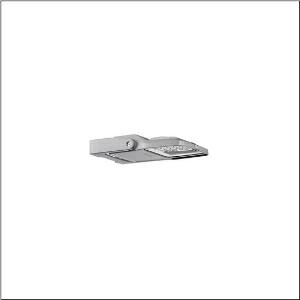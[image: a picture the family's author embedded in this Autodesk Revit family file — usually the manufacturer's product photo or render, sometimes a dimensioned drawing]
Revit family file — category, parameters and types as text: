
# Revit family: floodlight_fl_21_iq_micro___pl61_5xa7761a2c2a_8a4e
name_source: partatom
category: Lighting Fixtures
units: mm (PartAtom-declared; Revit-internal decimal feet)

## family parameters
Cut with Voids When Loaded = No
Host = Face
Light Source = No
Part Type = Normal
Room Calculation Point = No
Round Connector Dimension = Use Diameter
Shared = No

## types (1)
- --- (1 x LED, 2910 lm, 23.1 W, 3000K)
    Apparent Load = 23 VA
    CIE Flux Codes = 33 65 98 100 100
    Color Rendering = 70
    Color Temperature = 3000K
    Default Elevation = 1800 mm
    Description = Floodlight FL 21 iQ micro, floodlight, primary light control with lens, of PMMA, primary optical cover: protective disc, of toughened safety glass, transparent, light distribution: PL61, light emission: direct distribution, installation type: surface-mounted, LED, High Power LED, rated luminous flux: 2.910lm, luminous efficacy: 126lm/W, light colour: 730, colour temperature: 3000K, control: optimised constant luminous flux control (CLO 2.0), Desk-Remote (wireless, voltage-free reading and setting of iQ features in the workshop via application-optimized NFC function/RFID function), Light-Fading, Smart-Wire, Night-Set, Lumen-Switch, Temp-Guard, Auto-Match, with terminal, 6-pole, mains connection: 220..240V, AC, 50/60Hz, start of lifetime: 23W, end of service life: 24W, reduction: 11W, luminaire housing, of diecast aluminium, powder-coated, Siteco® metallic grey (DB 702S), corrosivity category C5 mid according to DIN EN ISO 12944, sealing non-destructively replaceable, design bracket, of diecast aluminium, powder-coated, Siteco® metallic grey (DB 702S), protection rating (complete): IP66, insulation class (complete): insulation class II (safety insulation), certification: CE, ENEC, VDE, protection symbol: D, impact resistance: IK07, permissible operating ambient temperature: -40..+40°C, permissible operating ambient temperature for outdoor applications: -40..+50°C, standard: DIN EN 12944, LABS conformity tested according to VDMA 24364:2018-05, packaging unit: 1 piece

Light Distribution: PL61
    Height = 65 mm
    Lamp = 1 x LED
    Lamp Light Flux = 2910 lm
    Lamp Power = 23.1 W
    Lamp count = 1
    Length = 312 mm
    Luminous efficacy = 126 lm/W
    Manufacturer = Siteco
    ModVariant = No
    Model = 5XA7761A2C2A
    Mounting Place = Wall
    Mounting Type = Surface mounted
    Number of Poles = 1
    OnlyDefault = Yes
    Power Factor = 1
    Product Name = Floodlight FL 21 iQ micro | PL61
    Product group = floodlight | wall mounted
    ProductGroupID = 2001
    Protection Class = Protection class II
    Protection Degree = IP 66
    RLX_Detail_Level = 1
    RLX_Emergency_Light_Flux = 0 lm
    RLX_Emergency_Type = 0
    RLX_Emergency_Type_DB = No
    RlxData = <blob elided: 97781 chars, md5=7267faca>
    Socket = socket
    Standby Power = 0 W
    System Light Flux = 2910 lm
    System Power = 23 W
    Type Comments = factory setting: luminous flux: 100 % | dim-lin: 254 | 455 mA
    Type Image = l_1006878.jpg
    URL = http://relux.com
    VarID = @adj_129163
    Voltage = 0 V
    Weight = 0.00 kg
    Width = 230 mm

## geometry (parser evidence)
native form markers: Blend x4, Sweep x12
no freeform markers — native parametric forms only
